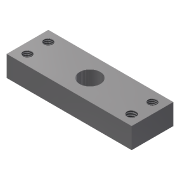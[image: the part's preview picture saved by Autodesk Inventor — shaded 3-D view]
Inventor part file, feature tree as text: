
AUTODESK INVENTOR PART (.ipt)
format: ipt  version: 2015 (Build 190159000, 159)  size: 123,392 bytes
history: native  units: mm
features: hole x5, extrude x1, sketch x1
ambient origin geometry x8: Origin, YZ Plane, XZ Plane, XY Plane, X Axis, Y Axis, Z Axis, Center Point
bodies: Body1 (feature_tree)
feature tree (7):
  extrude  "Extrusion2"  Depth=20.0mm
  hole  "Hole2"  [1 undecoded]
  hole  "Hole3"  [1 undecoded]
  hole  "Hole4"  [1 undecoded]
  hole  "Hole5"  [1 undecoded]
  hole  "Hole6"  [1 undecoded]
  sketch  "Sketch4"  dims[d37=60.0mm d38=20.0mm d39=10.0mm d40=0.0mm d41=10.0mm d42=30.0mm d43=10.0mm d44=6.0mm d45=10.5mm d46=6.5mm d47=90.0deg d48=10.0mm d49=20.594885mm d50=5.0mm d51=5.0mm d52=4.134mm d53=10.0mm d54=9.0mm d55=8.0mm d56=90.0deg d57=14.2mm d58=20.594885mm d59=5.0mm d60=5.0mm d61=4.134mm d62=10.0mm d63=9.0mm d64=8.0mm d65=90.0deg d66=14.2mm d67=20.594885mm d68=5.0mm d69=5.0mm d70=4.343mm d71=10.973mm d72=9.0mm d73=8.0mm d74=90.0deg d75=16.265mm d76=20.594885mm d77=5.0mm d78=5.0mm d79=4.134mm d80=10.0mm d81=9.0mm d82=8.0mm d83=90.0deg d84=14.2mm d85=20.594885mm]
note: 5 required parameter values undecoded (feature->parameter linkage not recoverable at this tier; creation-order binding heuristic only, values carry confidence <= 0.55)
